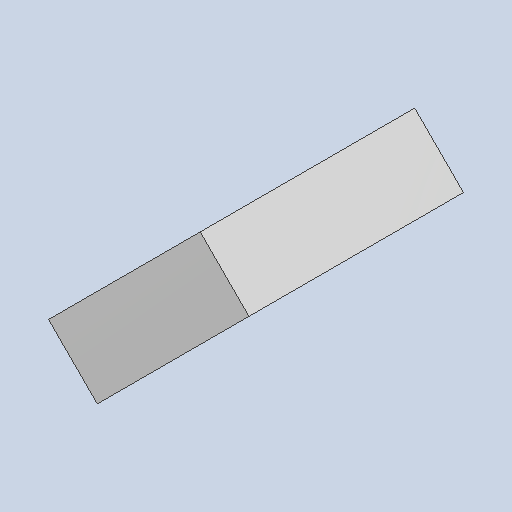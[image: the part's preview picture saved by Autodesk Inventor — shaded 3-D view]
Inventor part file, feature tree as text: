
AUTODESK INVENTOR PART (.ipt)
format: ipt  version: 2023.4 (Build 274418000, 418)  size: 79,360 bytes
history: native  units: mm
features: extrude x1
ambient origin geometry x8: Origin, YZ Plane, XZ Plane, XY Plane, X Axis, Y Axis, Z Axis, Center Point
bodies: Solid1 (feature_tree)
feature tree (1):
  extrude  "Extruded_1"  [1 undecoded]
note: 1 required parameter value undecoded (feature->parameter linkage not recoverable at this tier; creation-order binding heuristic only, values carry confidence <= 0.55)
